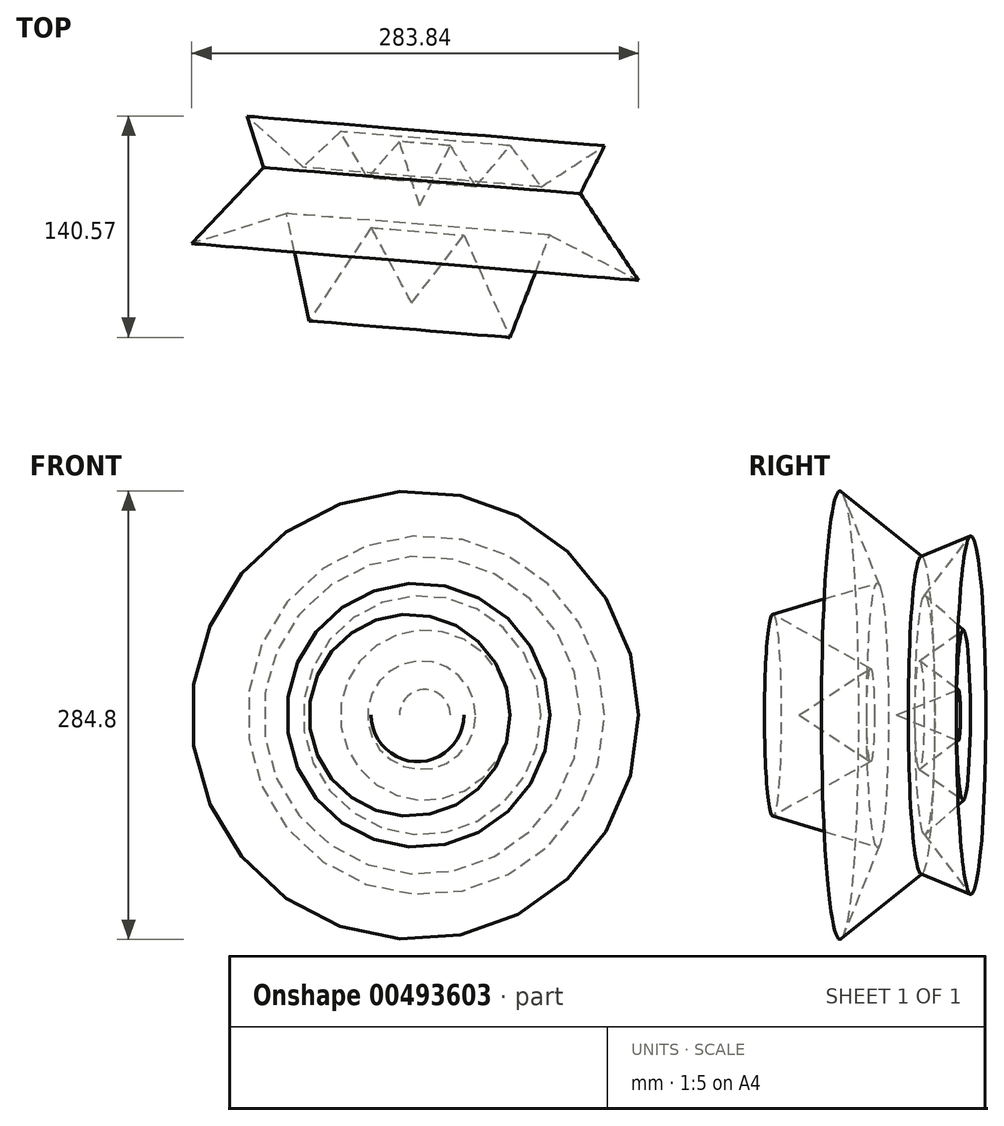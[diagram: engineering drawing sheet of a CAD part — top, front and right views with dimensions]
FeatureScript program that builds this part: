
annotation { "Feature Type Name" : "Feature", "Feature Type Description" : "" }
export const myFeature = defineFeature(function(context is Context, id is Id, definition is map)
    precondition{}
    {
        {
            var Q0;
            Q0=qCreatedBy(makeId("Top.planeOp"),FACE);
            var sketch = newSketch(context, id + "F0", { "sketchPlane" : qUnion([Q0])});
            skLineSegment(sketch, "E0", {"start": v(-67.12, 9.7) * mm, "end": v(-47.69, 47.8) * mm});
            skLineSegment(sketch, "E1", {"start": v(-47.69, 47.8) * mm, "end": v(-31.56, 21.65) * mm});
            skLineSegment(sketch, "E2", {"start": v(-31.56, 21.65) * mm, "end": v(-9.73, 47.8) * mm});
            skLineSegment(sketch, "E3", {"start": v(-9.73, 47.8) * mm, "end": v(9.99, 21.65) * mm});
            skLineSegment(sketch, "E4", {"start": v(9.99, 21.65) * mm, "end": v(50.35, 47.8) * mm});
            skLineSegment(sketch, "E5", {"start": v(50.35, 47.8) * mm, "end": v(34.82, 17.36) * mm});
            skLineSegment(sketch, "E6", {"start": v(34.82, 17.36) * mm, "end": v(71.84, -37.8) * mm});
            skLineSegment(sketch, "E7", {"start": v(71.84, -37.8) * mm, "end": v(15.48, -9.05) * mm});
            skLineSegment(sketch, "E8", {"start": v(15.48, -9.05) * mm, "end": v(-9.77, -74) * mm});
            skLineSegment(sketch, "E9", {"start": v(-9.77, -74) * mm, "end": v(-39.04, -9.05) * mm});
            skLineSegment(sketch, "E10", {"start": v(-39.04, -9.05) * mm, "end": v(-72.23, -52.1) * mm});
            skLineSegment(sketch, "E11", {"start": v(-72.23, -52.1) * mm, "end": v(-67.12, 9.7) * mm});
            skSolve(sketch);
        }
        {
            var Q0;
            Q0=makeQuery(id+"F0.imprint","IMPRINT",FACE,{"disambiguationData":[TD([[makeQuery(id+"F0.imprint","IMPRINT",EDGE,{"derivedFrom":sQuery(id+"F0.wireOp",EDGE,"E0")}),-1.0]])]});
            var Q1;
            Q1=sQuery(id+"F0.wireOp",EDGE,"E11");
            revolve(context, id + "F1", {"entities" : qUnion([Q0]), "axis" : qUnion([Q1]), "revolveType" : RevolveType.FULL});
        }
    });
